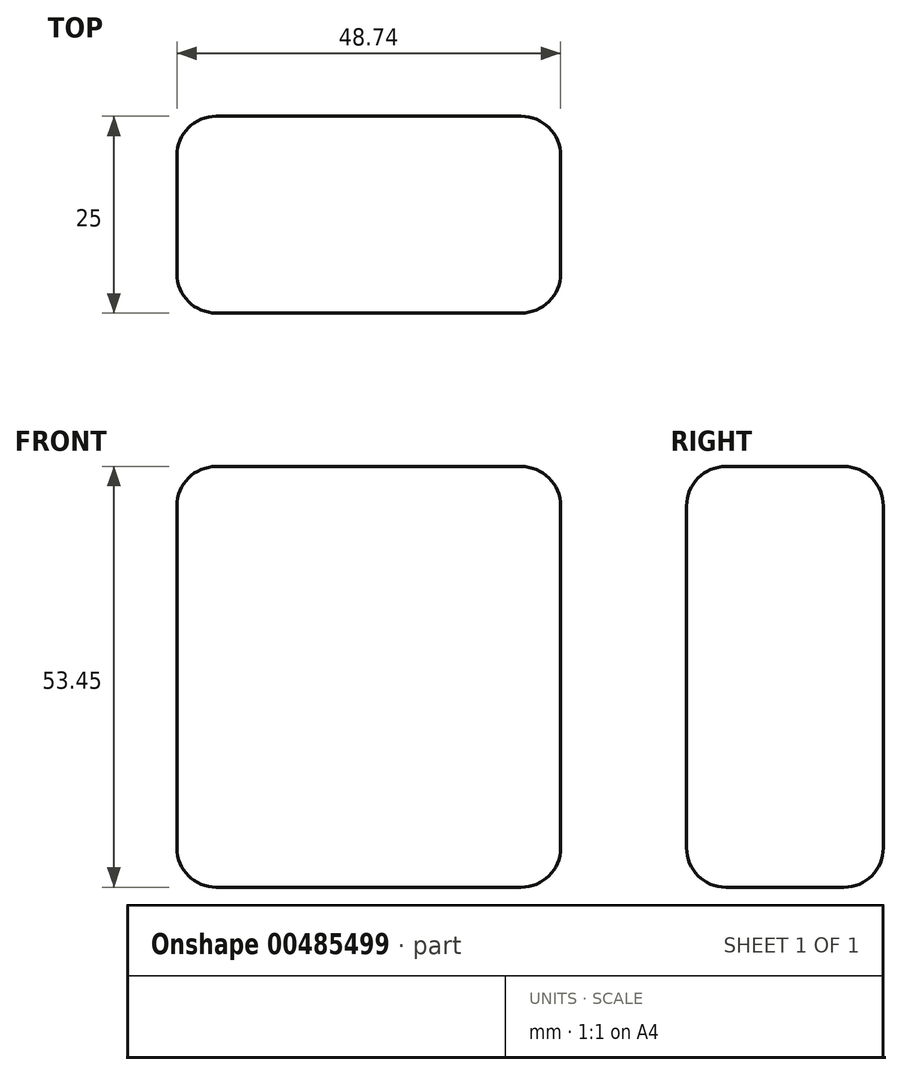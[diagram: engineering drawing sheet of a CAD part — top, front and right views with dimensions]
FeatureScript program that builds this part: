
annotation { "Feature Type Name" : "Feature", "Feature Type Description" : "" }
export const myFeature = defineFeature(function(context is Context, id is Id, definition is map)
    precondition{}
    {
        {
            var Q0;
            Q0=qCreatedBy(makeId("Front.planeOp"),FACE);
            var sketch = newSketch(context, id + "F0", { "sketchPlane" : qUnion([Q0])});
            skLineSegment(sketch, "E0.bottom", {"start": v(-93.13, 24.19) * mm, "end": v(-44.4, 24.19) * mm});
            skLineSegment(sketch, "E0.top", {"start": v(-93.13, 77.64) * mm, "end": v(-44.4, 77.64) * mm});
            skLineSegment(sketch, "E0.left", {"start": v(-93.13, 24.19) * mm, "end": v(-93.13, 77.64) * mm});
            skLineSegment(sketch, "E0.right", {"start": v(-44.4, 24.19) * mm, "end": v(-44.4, 77.64) * mm});
            skPoint(sketch, "E0.middle", {"position": v(-68.76, 50.91) * mm});
            skSolve(sketch);
        }
        {
            var Q0;
            Q0=makeQuery(id+"F0.imprint","IMPRINT",FACE,{"disambiguationData":[TD([[makeQuery(id+"F0.imprint","IMPRINT",EDGE,{"derivedFrom":sQuery(id+"F0.wireOp",EDGE,"E0.bottom")}),1.0]])]});
            extrude(context, id + "F1", {"entities" : qUnion([Q0]), "depth" : 25 * mm});
        }
        {
            var Q0;
            Q0=makeQuery(id+"F1.opExtrude","SWEPT_EDGE",EDGE,{"disambiguationData":[OSD([sQuery(id+"F0.wireOp",EDGE,"E0.top"),sQuery(id+"F0.wireOp",EDGE,"E0.right")])]});
            var Q1;
            Q1=makeQuery(id+"F1.opExtrude","SWEPT_EDGE",EDGE,{"disambiguationData":[OSD([sQuery(id+"F0.wireOp",EDGE,"E0.top"),sQuery(id+"F0.wireOp",EDGE,"E0.left")])]});
            var Q2;
            Q2=makeQuery(id+"F1.opExtrude","SWEPT_EDGE",EDGE,{"disambiguationData":[OSD([sQuery(id+"F0.wireOp",EDGE,"E0.bottom"),sQuery(id+"F0.wireOp",EDGE,"E0.right")])]});
            var Q3;
            Q3=makeQuery(id+"F1.opExtrude","CAP_EDGE",EDGE,{"disambiguationData":[OSD([sQuery(id+"F0.wireOp",EDGE,"E0.bottom")])],"isStart":false});
            var Q4;
            Q4=makeQuery(id+"F1.opExtrude","CAP_EDGE",EDGE,{"disambiguationData":[OSD([sQuery(id+"F0.wireOp",EDGE,"E0.top")])],"isStart":true});
            var Q5;
            Q5=makeQuery(id+"F1.opExtrude","CAP_EDGE",EDGE,{"disambiguationData":[OSD([sQuery(id+"F0.wireOp",EDGE,"E0.top")])],"isStart":false});
            var Q6;
            Q6=makeQuery(id+"F1.opExtrude","SWEPT_EDGE",EDGE,{"disambiguationData":[OSD([sQuery(id+"F0.wireOp",EDGE,"E0.bottom"),sQuery(id+"F0.wireOp",EDGE,"E0.left")])]});
            var Q7;
            Q7=makeQuery(id+"F1.opExtrude","CAP_EDGE",EDGE,{"disambiguationData":[OSD([sQuery(id+"F0.wireOp",EDGE,"E0.bottom")])],"isStart":true});
            var Q8;
            Q8=makeQuery(id+"F1.opExtrude","CAP_EDGE",EDGE,{"disambiguationData":[OSD([sQuery(id+"F0.wireOp",EDGE,"E0.left")])],"isStart":true});
            var Q9;
            Q9=makeQuery(id+"F1.opExtrude","CAP_EDGE",EDGE,{"disambiguationData":[OSD([sQuery(id+"F0.wireOp",EDGE,"E0.left")])],"isStart":false});
            var Q10;
            Q10=makeQuery(id+"F1.opExtrude","CAP_EDGE",EDGE,{"disambiguationData":[OSD([sQuery(id+"F0.wireOp",EDGE,"E0.right")])],"isStart":true});
            var Q11;
            Q11=makeQuery(id+"F1.opExtrude","CAP_EDGE",EDGE,{"disambiguationData":[OSD([sQuery(id+"F0.wireOp",EDGE,"E0.right")])],"isStart":false});
            fillet(context, id + "F2", {"entities" : qUnion([Q0, Q1, Q2, Q3, Q4, Q5, Q6, Q7, Q8, Q9, Q10, Q11]), "radius" : 5 * mm, "tangentPropagation" : true, "allowEdgeOverflow" : false});
        }
    });
